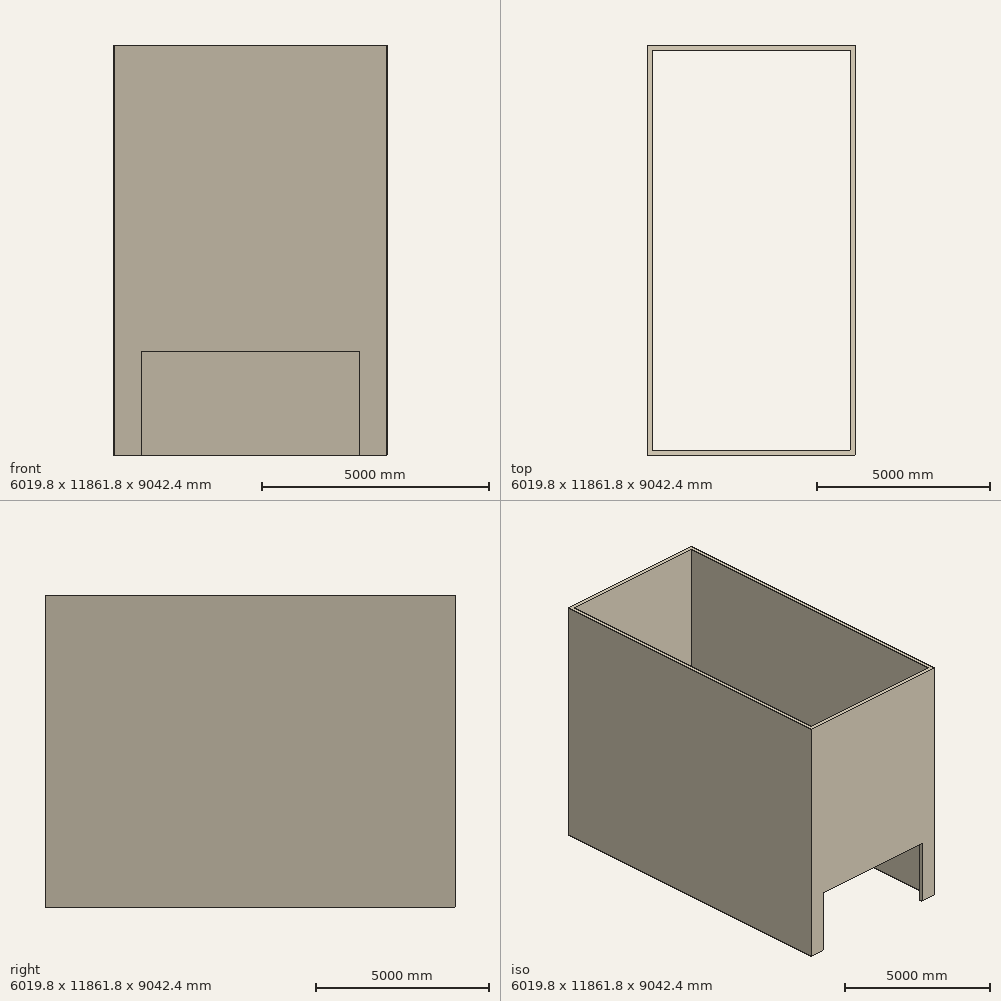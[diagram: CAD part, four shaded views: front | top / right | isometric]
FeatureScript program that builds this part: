
annotation { "Feature Type Name" : "Feature", "Feature Type Description" : "" }
export const myFeature = defineFeature(function(context is Context, id is Id, definition is map)
    precondition{}
    {
        {
            var Q0;
            Q0=qCreatedBy(makeId("Top.planeOp"),FACE);
            var sketch = newSketch(context, id + "F0", { "sketchPlane" : qUnion([Q0])});
            skLineSegment(sketch, "E0.bottom", {"start": v(-3009.9, 5930.9) * mm, "end": v(3009.9, 5930.9) * mm});
            skLineSegment(sketch, "E0.top", {"start": v(-3009.9, -5930.9) * mm, "end": v(3009.9, -5930.9) * mm});
            skLineSegment(sketch, "E0.left", {"start": v(-3009.9, 5930.9) * mm, "end": v(-3009.9, -5930.9) * mm});
            skLineSegment(sketch, "E0.right", {"start": v(3009.9, 5930.9) * mm, "end": v(3009.9, -5930.9) * mm});
            skLineSegment(sketch, "E1", {"start": v(-2857.5, 5778.5) * mm, "end": v(2857.5, 5778.5) * mm});
            skLineSegment(sketch, "E2", {"start": v(2857.5, 5778.5) * mm, "end": v(2857.5, -5778.5) * mm});
            skLineSegment(sketch, "E3", {"start": v(-2857.5, -5778.5) * mm, "end": v(-2857.5, 5778.5) * mm});
            skLineSegment(sketch, "E4", {"start": v(2857.5, -5778.5) * mm, "end": v(-2857.5, -5778.5) * mm});
            skSolve(sketch);
        }
        {
            var Q0;
            Q0=makeQuery(id+"F0.imprint","IMPRINT",FACE,{"disambiguationData":[TD([[makeQuery(id+"F0.imprint","IMPRINT",EDGE,{"derivedFrom":sQuery(id+"F0.wireOp",EDGE,"E0.bottom")}),-1.0]])]});
            extrude(context, id + "F1", {"entities" : qUnion([Q0]), "depth" : 9042.4 * mm});
        }
        {
            var Q0;
            Q0=makeQuery(id+"F1.opExtrude","SWEPT_FACE",FACE,{"disambiguationData":[OSD([sQuery(id+"F0.wireOp",EDGE,"E0.top")])]});
            var sketch = newSketch(context, id + "F2", { "sketchPlane" : qUnion([Q0])});
            skLineSegment(sketch, "E5", {"start": v(-2400.3, 0) * mm, "end": v(-2400.3, 2286) * mm});
            skLineSegment(sketch, "E6", {"start": v(-2400.3, 2286) * mm, "end": v(2400.3, 2286) * mm});
            skLineSegment(sketch, "E7", {"start": v(2400.3, 2286) * mm, "end": v(2400.3, 0) * mm});
            skSolve(sketch);
        }
        {
            var Q0;
            {var subQ0=sQuery(id+"F2.wireOp",EDGE,"E5");Q0=makeQuery(id+"F2.imprint","IMPRINT",FACE,{"disambiguationData":[TD([[makeQuery(id+"F2.imprint","IMPRINT",EDGE,{"derivedFrom":subQ0}),-1.0]])]});}
            extrude(context, id + "F3", {"entities" : qUnion([Q0]), "operationType" : NewBodyOperationType.REMOVE, "endBound" : BoundingType.UP_TO_NEXT, "oppositeDirection" : true, "depth" : 25.4 * mm});
        }
    });
